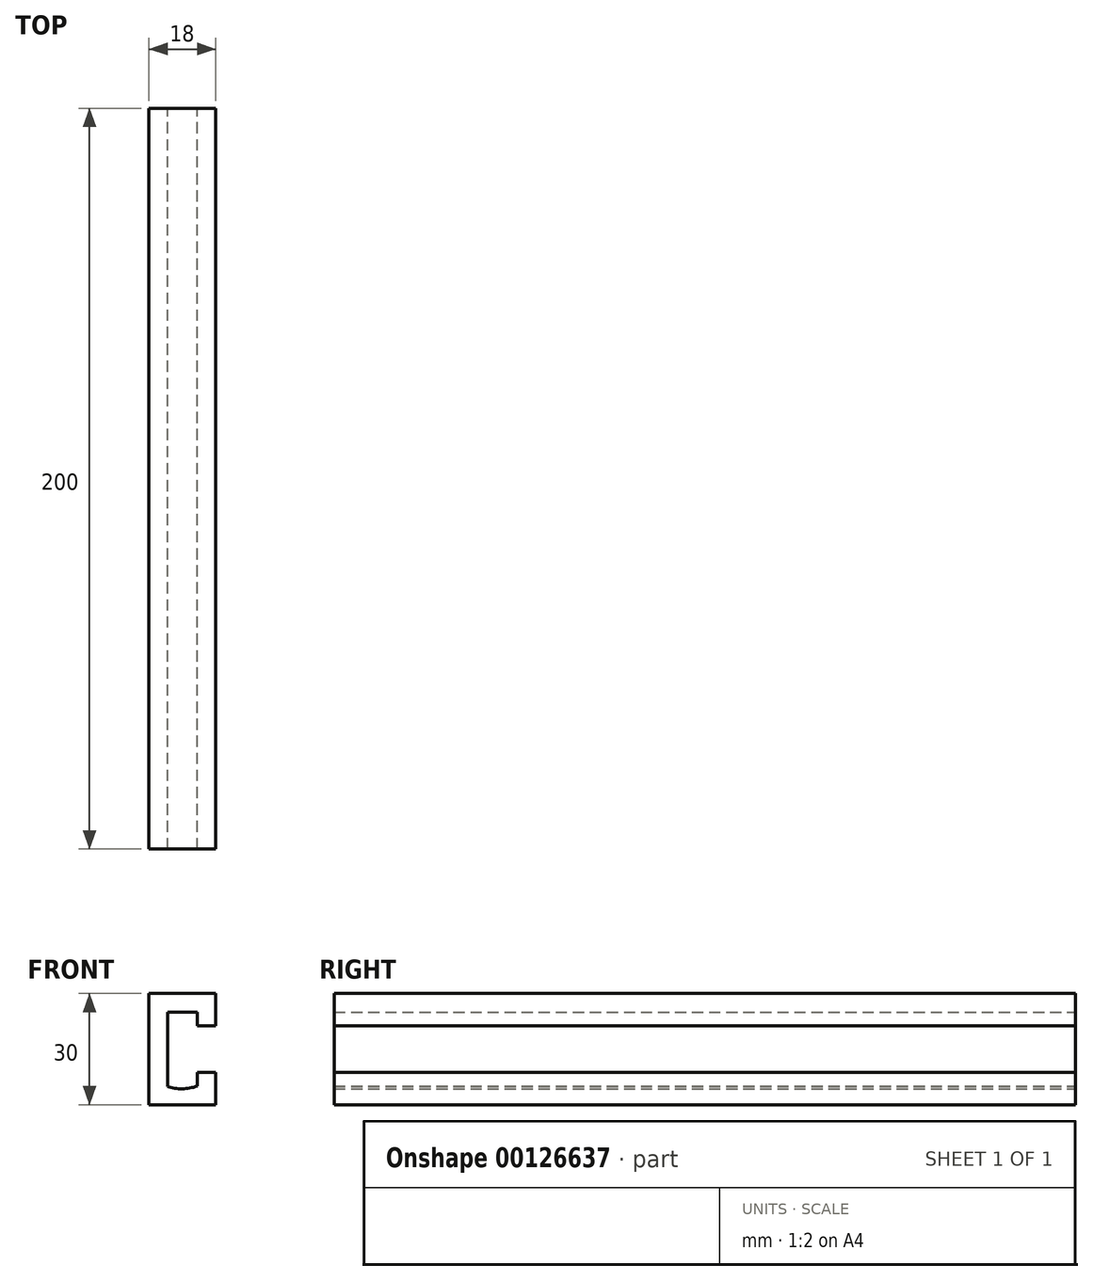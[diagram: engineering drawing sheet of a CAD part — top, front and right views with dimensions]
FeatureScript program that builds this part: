
annotation { "Feature Type Name" : "Feature", "Feature Type Description" : "" }
export const myFeature = defineFeature(function(context is Context, id is Id, definition is map)
    precondition{}
    {
        {
            var Q0;
            Q0=qCreatedBy(makeId("Front.planeOp"),FACE);
            var sketch = newSketch(context, id + "F0", { "sketchPlane" : qUnion([Q0])});
            skLineSegment(sketch, "E0", {"start": v(0, 15) * mm, "end": v(-18, 15) * mm});
            skLineSegment(sketch, "E1", {"start": v(-18, 15) * mm, "end": v(-18, -15) * mm});
            skLineSegment(sketch, "E2", {"start": v(-18, -15) * mm, "end": v(0, -15) * mm});
            skLineSegment(sketch, "E3", {"start": v(-13, -10.13) * mm, "end": v(-13, 10) * mm});
            skLineSegment(sketch, "E4", {"start": v(0, 15) * mm, "end": v(0, 6.25) * mm});
            skLineSegment(sketch, "E5", {"start": v(0, 6.25) * mm, "end": v(-5, 6.25) * mm});
            skLineSegment(sketch, "E6", {"start": v(-5, 6.25) * mm, "end": v(-5, 10) * mm});
            skLineSegment(sketch, "E7", {"start": v(-5, 10) * mm, "end": v(-13, 10) * mm});
            skLineSegment(sketch, "E8", {"start": v(-5, -10) * mm, "end": v(-5, -6.25) * mm});
            skLineSegment(sketch, "E9", {"start": v(-5, -6.25) * mm, "end": v(0, -6.25) * mm});
            skLineSegment(sketch, "E10", {"start": v(0, -6.25) * mm, "end": v(0, -15) * mm});
            skArc(sketch, "E11", {"start": v(-13, -10.13) * mm, "mid": v(-8.99, -10.7) * mm, "end": v(-5, -10) * mm});
            skSolve(sketch);
        }
        {
            var Q0;
            Q0=makeQuery(id+"F0.imprint","IMPRINT",FACE,{"disambiguationData":[TD([[makeQuery(id+"F0.imprint","IMPRINT",EDGE,{"derivedFrom":sQuery(id+"F0.wireOp",EDGE,"E0")}),1.0]])]});
            extrude(context, id + "F1", {"entities" : qUnion([Q0]), "endBound" : BoundingType.SYMMETRIC, "depth" : 200 * mm});
        }
    });
